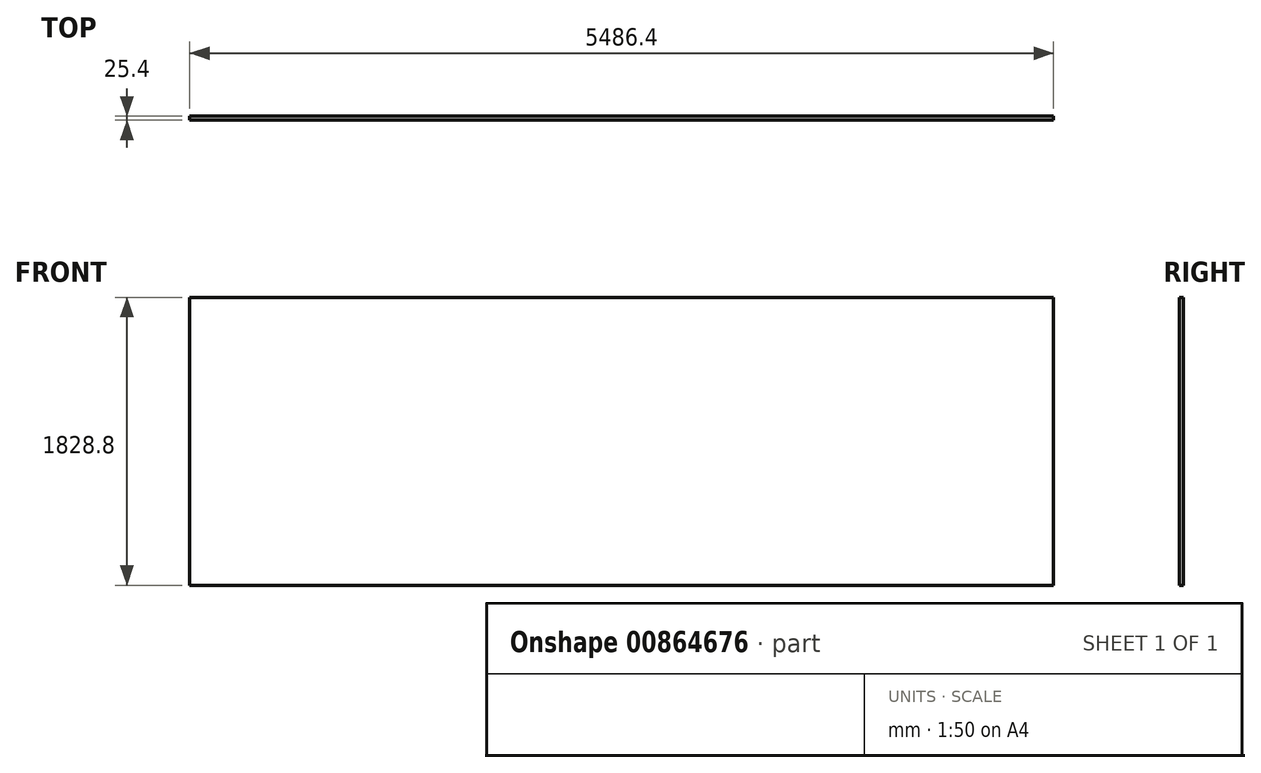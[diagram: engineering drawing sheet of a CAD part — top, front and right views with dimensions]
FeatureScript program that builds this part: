
annotation { "Feature Type Name" : "Feature", "Feature Type Description" : "" }
export const myFeature = defineFeature(function(context is Context, id is Id, definition is map)
    precondition{}
    {
        {
            var Q0;
            Q0=qCreatedBy(makeId("Front.planeOp"),FACE);
            var sketch = newSketch(context, id + "F0", { "sketchPlane" : qUnion([Q0])});
            skLineSegment(sketch, "E0", {"start": v(0, 0) * mm, "end": v(5486.4, 0) * mm});
            skLineSegment(sketch, "E1", {"start": v(5486.4, 0) * mm, "end": v(5486.4, 1828.8) * mm});
            skLineSegment(sketch, "E2", {"start": v(5486.4, 1828.8) * mm, "end": v(0, 1828.8) * mm});
            skLineSegment(sketch, "E3", {"start": v(0, 1828.8) * mm, "end": v(0, 0) * mm});
            skSolve(sketch);
        }
        {
            var Q0;
            Q0=makeQuery(id+"F0.imprint","IMPRINT",FACE,{"disambiguationData":[TD([[makeQuery(id+"F0.imprint","IMPRINT",EDGE,{"derivedFrom":sQuery(id+"F0.wireOp",EDGE,"E0")}),1.0]])]});
            extrude(context, id + "F1", {"entities" : qUnion([Q0]), "depth" : 25.4 * mm, "offsetDistance" : 25.4 * mm});
        }
    });
